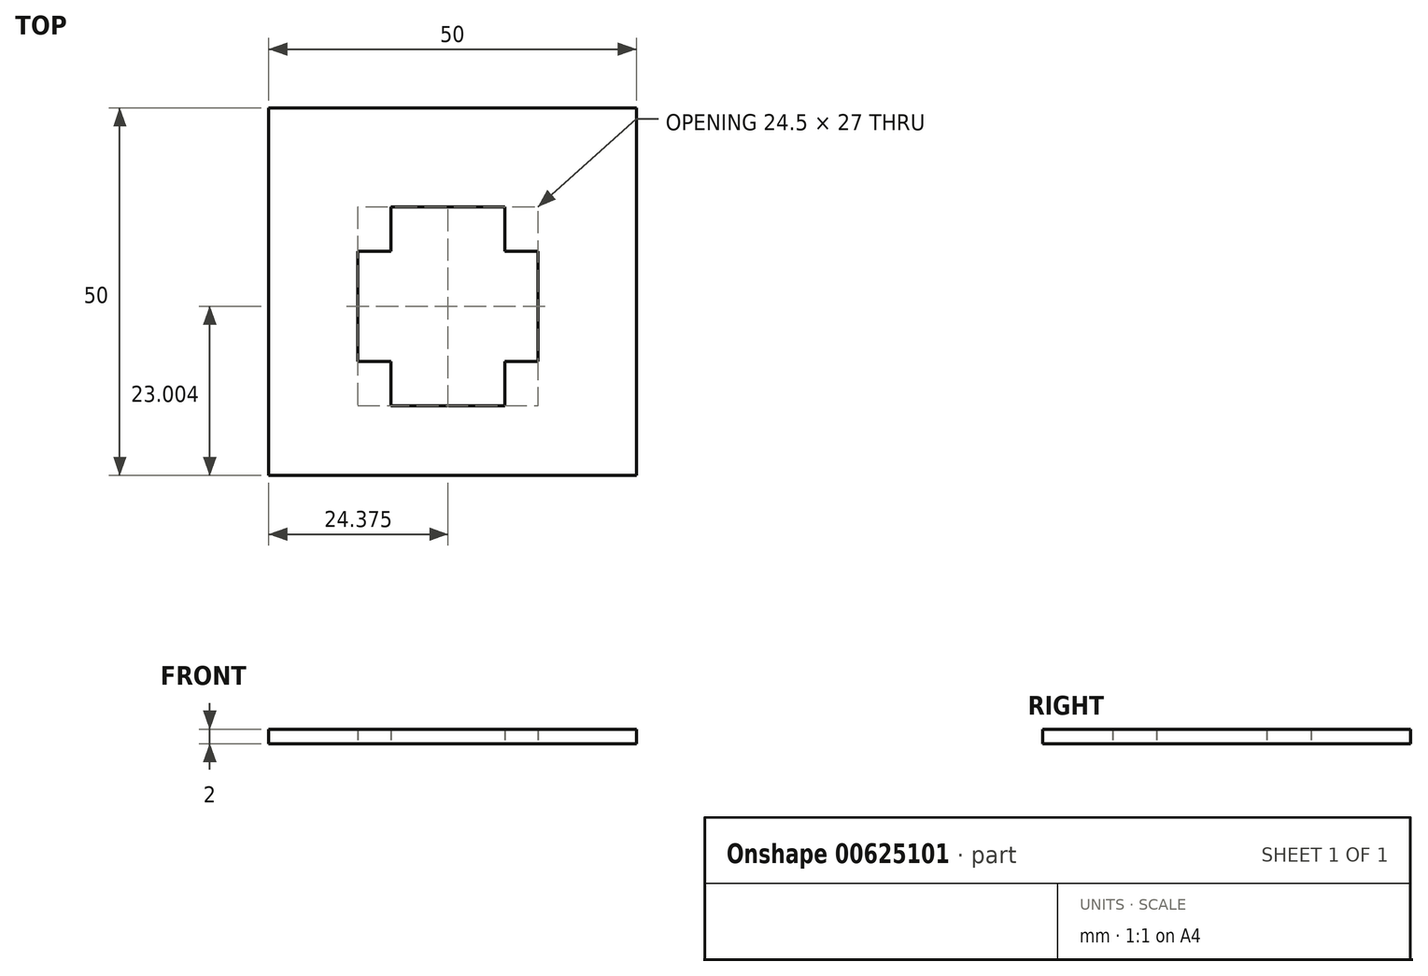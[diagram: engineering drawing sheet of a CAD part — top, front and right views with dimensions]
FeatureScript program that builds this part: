
annotation { "Feature Type Name" : "Feature", "Feature Type Description" : "" }
export const myFeature = defineFeature(function(context is Context, id is Id, definition is map)
    precondition{}
    {
        {
            var Q0;
            Q0=qCreatedBy(makeId("Top.planeOp"),FACE);
            var sketch = newSketch(context, id + "F0", { "sketchPlane" : qUnion([Q0])});
            skLineSegment(sketch, "E0.bottom", {"start": v(-24.24, 25.68) * mm, "end": v(25.76, 25.68) * mm});
            skLineSegment(sketch, "E0.top", {"start": v(-24.24, -24.32) * mm, "end": v(25.76, -24.32) * mm});
            skLineSegment(sketch, "E0.left", {"start": v(-24.24, 25.68) * mm, "end": v(-24.24, -24.32) * mm});
            skLineSegment(sketch, "E0.right", {"start": v(25.76, 25.68) * mm, "end": v(25.76, -24.32) * mm});
            skSolve(sketch);
        }
        {
            var Q0;
            Q0=makeQuery(id+"F0.imprint","IMPRINT",FACE,{"disambiguationData":[TD([[makeQuery(id+"F0.imprint","IMPRINT",EDGE,{"derivedFrom":sQuery(id+"F0.wireOp",EDGE,"E0.bottom")}),-1.0]])]});
            extrude(context, id + "F1", {"entities" : qUnion([Q0]), "depth" : 2 * mm, "offsetDistance" : 25 * mm});
        }
        {
            var Q0;
            Q0=qCreatedBy(makeId("Top.planeOp"),FACE);
            var sketch = newSketch(context, id + "F2", { "sketchPlane" : qUnion([Q0])});
            skLineSegment(sketch, "E1", {"start": v(-7.61, 12.18) * mm, "end": v(7.89, 12.18) * mm});
            skLineSegment(sketch, "E2", {"start": v(7.89, 6.18) * mm, "end": v(7.89, 12.18) * mm});
            skLineSegment(sketch, "E3", {"start": v(-7.61, 12.18) * mm, "end": v(-7.61, 6.18) * mm});
            skLineSegment(sketch, "E4", {"start": v(-7.61, 6.18) * mm, "end": v(-12.11, 6.18) * mm});
            skLineSegment(sketch, "E5", {"start": v(-12.11, 6.18) * mm, "end": v(-12.11, -8.82) * mm});
            skLineSegment(sketch, "E6", {"start": v(-12.11, -8.82) * mm, "end": v(-7.61, -8.82) * mm});
            skLineSegment(sketch, "E7", {"start": v(-7.61, -8.82) * mm, "end": v(-7.61, -14.82) * mm});
            skLineSegment(sketch, "E8", {"start": v(-7.61, -14.82) * mm, "end": v(7.89, -14.82) * mm});
            skLineSegment(sketch, "E9", {"start": v(7.89, -14.82) * mm, "end": v(7.89, -8.82) * mm});
            skLineSegment(sketch, "E10", {"start": v(7.89, -8.82) * mm, "end": v(12.39, -8.82) * mm});
            skLineSegment(sketch, "E11", {"start": v(12.39, -8.82) * mm, "end": v(12.39, 6.18) * mm});
            skLineSegment(sketch, "E12", {"start": v(12.39, 6.18) * mm, "end": v(7.89, 6.18) * mm});
            skSolve(sketch);
        }
        {
            var Q0;
            Q0=makeQuery(id+"F2.imprint","IMPRINT",FACE,{"disambiguationData":[TD([[makeQuery(id+"F2.imprint","IMPRINT",EDGE,{"derivedFrom":sQuery(id+"F2.wireOp",EDGE,"E1")}),-1.0]])]});
            extrude(context, id + "F3", {"entities" : qUnion([Q0]), "depth" : 25 * mm, "offsetDistance" : 25 * mm});
        }
        {
            var Q0;
            Q0=makeQuery(id+"F3.opExtrude","SWEPT_BODY",BODY,{"disambiguationData":[OSD([sQuery(id+"F2.wireOp",EDGE,"E1"),sQuery(id+"F2.wireOp",EDGE,"E2"),sQuery(id+"F2.wireOp",EDGE,"E3"),sQuery(id+"F2.wireOp",EDGE,"E4"),sQuery(id+"F2.wireOp",EDGE,"E5"),sQuery(id+"F2.wireOp",EDGE,"E6"),sQuery(id+"F2.wireOp",EDGE,"E7"),sQuery(id+"F2.wireOp",EDGE,"E8"),sQuery(id+"F2.wireOp",EDGE,"E9"),sQuery(id+"F2.wireOp",EDGE,"E10"),sQuery(id+"F2.wireOp",EDGE,"E11"),sQuery(id+"F2.wireOp",EDGE,"E12")])]});
            var Q1;
            Q1=makeQuery(id+"F1.opExtrude","SWEPT_BODY",BODY,{"disambiguationData":[OSD([sQuery(id+"F0.wireOp",EDGE,"E0.bottom"),sQuery(id+"F0.wireOp",EDGE,"E0.top"),sQuery(id+"F0.wireOp",EDGE,"E0.left"),sQuery(id+"F0.wireOp",EDGE,"E0.right")])]});
            booleanBodies(context, id + "F4", {"operationType" : BooleanOperationType.SUBTRACTION, "tools" : qUnion([Q0]), "targets" : qUnion([Q1])});
        }
    });
